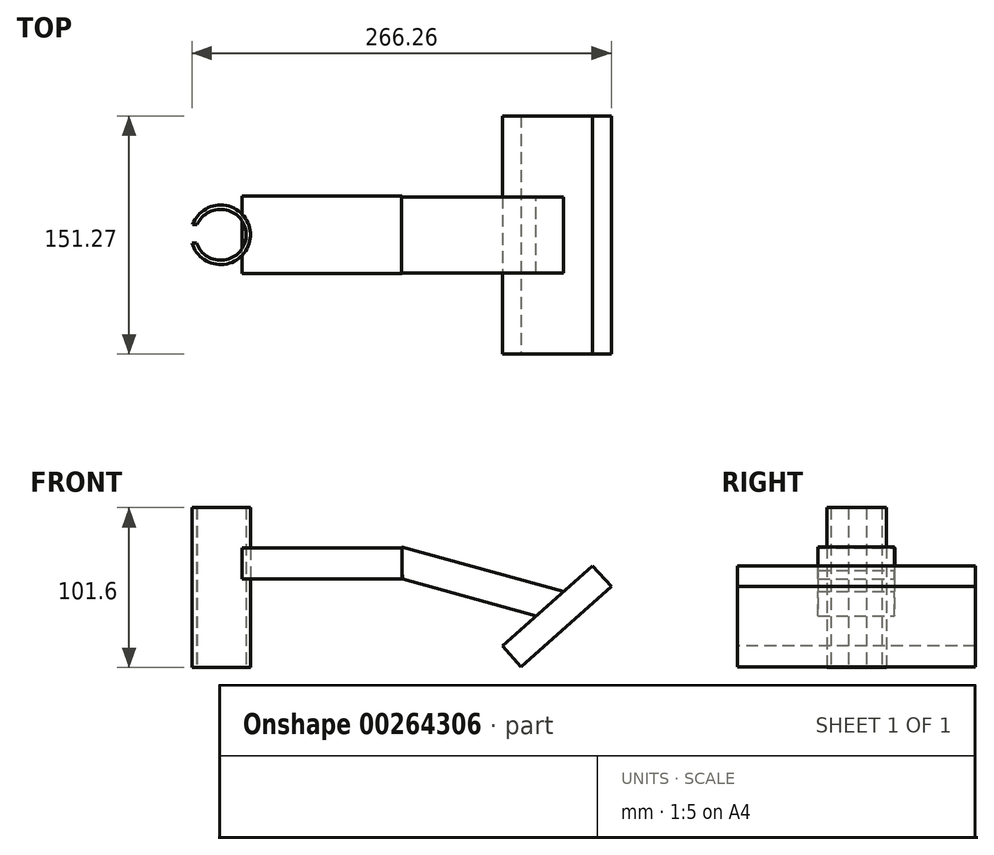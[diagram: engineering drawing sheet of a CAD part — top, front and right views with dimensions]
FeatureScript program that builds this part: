
annotation { "Feature Type Name" : "Feature", "Feature Type Description" : "" }
export const myFeature = defineFeature(function(context is Context, id is Id, definition is map)
    precondition{}
    {
        {
            var Q0;
            Q0=qCreatedBy(makeId("Top.planeOp"),FACE);
            var sketch = newSketch(context, id + "F0", { "sketchPlane" : qUnion([Q0])});
            skArc(sketch, "E0", {"start": v(-28.95, -5.2) * mm, "mid": v(2.53, -0.66) * mm, "end": v(-28.47, 6.44) * mm});
            skArc(sketch, "E1", {"start": v(-31.8, -5.2) * mm, "mid": v(5.26, -0.65) * mm, "end": v(-31.4, 6.44) * mm});
            skLineSegment(sketch, "E2", {"start": v(-31.8, -5.2) * mm, "end": v(-28.95, -5.2) * mm});
            skLineSegment(sketch, "E3", {"start": v(-31.4, 6.44) * mm, "end": v(-28.47, 6.44) * mm});
            skSolve(sketch);
        }
        {
            var Q0;
            Q0 = qSketchRegion(id + "F0", true);
            extrude(context, id + "F1", {"entities" : qUnion([Q0]), "depth" : 101.6 * mm});
        }
        {
            var Q0;
            Q0=qCreatedBy(makeId("Right.planeOp"),FACE);
            var sketch = newSketch(context, id + "F2", { "sketchPlane" : qUnion([Q0])});
            skLineSegment(sketch, "E4.bottom", {"start": v(-24.56, 56.21) * mm, "end": v(24.56, 56.21) * mm});
            skLineSegment(sketch, "E4.top", {"start": v(-24.56, 75.87) * mm, "end": v(24.56, 75.87) * mm});
            skLineSegment(sketch, "E4.left", {"start": v(-24.56, 56.21) * mm, "end": v(-24.56, 75.87) * mm});
            skLineSegment(sketch, "E4.right", {"start": v(24.56, 56.21) * mm, "end": v(24.56, 75.87) * mm});
            skSolve(sketch);
        }
        {
            var Q0;
            Q0 = qSketchRegion(id + "F2", true);
            extrude(context, id + "F3", {"entities" : qUnion([Q0]), "depth" : 101.6 * mm});
        }
        {
            var Q0;
            Q0=qCreatedBy(makeId("Front.planeOp"),FACE);
            var sketch = newSketch(context, id + "F4", { "sketchPlane" : qUnion([Q0])});
            skLineSegment(sketch, "E5", {"start": v(101.76, 56.17) * mm, "end": v(186.75, 32.69) * mm});
            skLineSegment(sketch, "E6", {"start": v(101.16, 76.67) * mm, "end": v(204.15, 48.21) * mm});
            skLineSegment(sketch, "E7", {"start": v(186.75, 32.69) * mm, "end": v(204.15, 48.21) * mm});
            skLineSegment(sketch, "E8", {"start": v(101.76, 56.17) * mm, "end": v(101.16, 76.67) * mm});
            skSolve(sketch);
        }
        {
            var Q0;
            Q0 = qSketchRegion(id + "F4", true);
            extrude(context, id + "F5", {"entities" : qUnion([Q0]), "operationType" : NewBodyOperationType.ADD, "depth" : 24.38 * mm, "hasSecondDirection" : true, "secondDirectionOppositeDirection" : true, "secondDirectionDepth" : 24.13 * mm});
        }
        {
            var Q0;
            Q0=makeQuery(id+"F5.opExtrude","SWEPT_FACE",FACE,{"disambiguationData":[OSD([sQuery(id+"F4.wireOp",EDGE,"E7")])]});
            var sketch = newSketch(context, id + "F6", { "sketchPlane" : qUnion([Q0])});
            skLineSegment(sketch, "E9.bottom", {"start": v(209.18, -75.5) * mm, "end": v(132.42, -75.5) * mm});
            skLineSegment(sketch, "E9.top", {"start": v(209.18, 75.76) * mm, "end": v(132.42, 75.76) * mm});
            skLineSegment(sketch, "E9.left", {"start": v(209.18, -75.5) * mm, "end": v(209.18, 75.76) * mm});
            skLineSegment(sketch, "E9.right", {"start": v(132.42, -75.5) * mm, "end": v(132.42, 75.76) * mm});
            skPoint(sketch, "E9.middle", {"position": v(170.8, 0.13) * mm});
            skPoint(sketch, "E9.middle.positionSnap0", {"position": v(184.41, 0.13) * mm});
            skPoint(sketch, "E9.centerSnap0", {"position": v(184.41, 0.13) * mm});
            skSolve(sketch);
        }
        {
            var Q0;
            Q0 = qSketchRegion(id + "F6", true);
            extrude(context, id + "F7", {"entities" : qUnion([Q0]), "operationType" : NewBodyOperationType.ADD, "depth" : 17.78 * mm});
        }
    });
